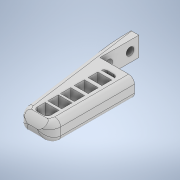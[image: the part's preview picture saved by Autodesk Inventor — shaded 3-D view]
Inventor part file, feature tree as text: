
AUTODESK INVENTOR PART (.ipt)
format: ipt  version: 2021 (Build 250183000, 183)  size: 287,232 bytes
history: native  units: mm
features: move_body x6, extrude x5, direct_edit x5, sketch x5, other x4, fillet x3, reference x2, projected_geometry x2
ambient origin geometry x8: Origin, YZ Plane, XZ Plane, XY Plane, X Axis, Y Axis, Z Axis, Center Point
bodies: Solid1 (feature_tree)
feature tree (32):
  extrude  "Extrusion1"  Depth=20.0mm
  extrude  "Extrusion2"  Depth=12.0mm
  direct_edit  "Direct Edit1"
  direct_edit  "Direct Edit2"
  direct_edit  "Direct Edit3"
  extrude  "Extrusion3"  Depth=10.0mm
  direct_edit  "Direct Edit4"
  fillet  "Fillet1"  Radius=10.0mm
  extrude  "Extrusion4"  Depth=10.0mm TaperAngle=0.0deg
  fillet  "Fillet2"  Radius=10.0mm
  fillet  "Fillet3"  Radius=2.0mm
  extrude  "Extrusion5"  Depth=10.0mm TaperAngle=0.0deg
  direct_edit  "Direct Edit5"
  sketch  "Sketch1"  dims[d0=4.0mm d1=20.0mm]
  sketch  "Sketch2"  dims[d2=14.0mm d3=12.0mm]
  reference  "Reference1"
  reference  "Reference2"
  sketch  "Sketch3"  dims[d4=12.0mm d5=12.0mm d6=10.0mm]
  sketch  "Sketch4"  dims[d7=20.0mm d8=10.0mm d9=0.0mm d10=10.0mm d11=0.0mm]
  projected_geometry  "Projected Loop1"
  projected_geometry  "Projected Loop2"
  sketch  "Sketch5"  dims[d12=0.0mm d13=0.0mm d14=7.0mm d15=0.0mm d16=0.0mm d17=2.0mm d18=0.0mm d19=0.0mm d20=8.0mm d21=0.0mm d22=0.0mm d23=7.75mm d24=10.0mm d25=0.0mm d26=0.0mm d27=0.0mm d28=0.5mm d29=2.0mm d30=30.5mm d31=0.0mm d32=6.0mm d33=3.0mm d34=10.0mm d35=0.0mm d36=1.25mm d37=0.0mm d38=0.5mm]
  parser-record x1  (decoder bookkeeping rows leaked as tree rows — omitted from the tree; the rows remain in map.json)
  other  "whole_assembly.iam"
  other  "539636 HGP-16-A-B-SSK---(asm_0_-ZH):1"
  other  "HGP-16---(116_JAW):2"
  move_body  "Move1"
  move_body  "Move2"
  move_body  "Move3"
  move_body  "Move4"
  move_body  "Move5"
  move_body  "Move6"
note: 1 file-system path scrubbed to <path> (originals preserved in map.json)
